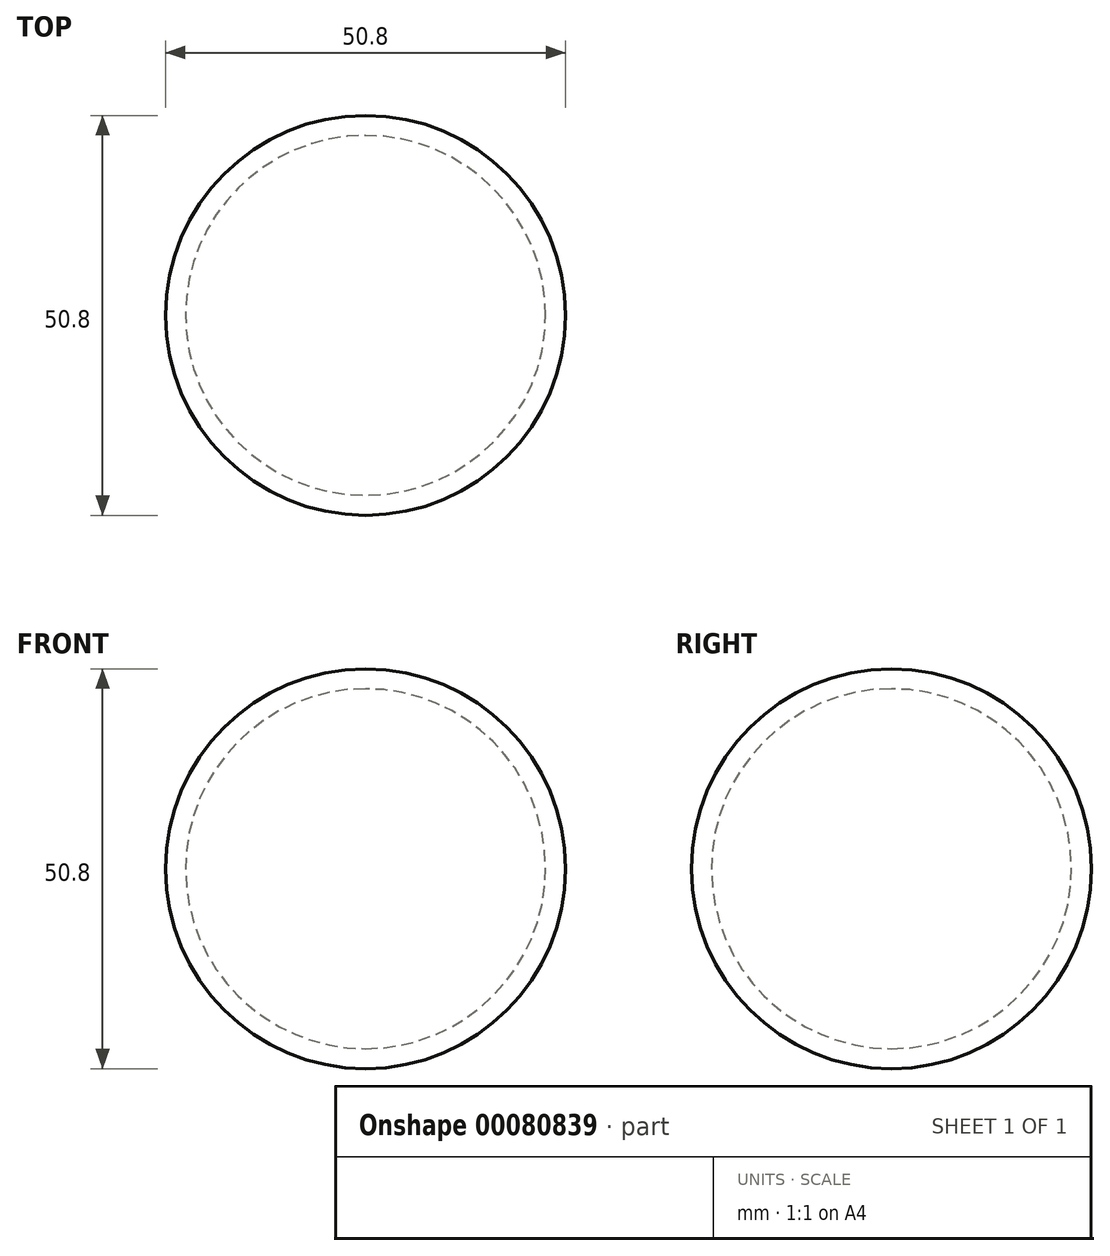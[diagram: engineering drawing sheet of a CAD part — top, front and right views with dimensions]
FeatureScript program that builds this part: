
annotation { "Feature Type Name" : "Feature", "Feature Type Description" : "" }
export const myFeature = defineFeature(function(context is Context, id is Id, definition is map)
    precondition{}
    {
        {
            var Q0;
            Q0=qCreatedBy(makeId("Front.planeOp"),FACE);
            var sketch = newSketch(context, id + "F0", { "sketchPlane" : qUnion([Q0])});
            skArc(sketch, "E0", {"start": v(0, 25.4) * mm, "mid": v(25.4, 0) * mm, "end": v(0, -25.4) * mm});
            skLineSegment(sketch, "E1", {"start": v(0, 25.4) * mm, "end": v(0, -25.4) * mm, "construction": true});
            skArc(sketch, "E2.0", {"start": v(0, 22.86) * mm, "mid": v(22.86, 0) * mm, "end": v(0, -22.86) * mm});
            skLineSegment(sketch, "E3", {"start": v(0, 25.4) * mm, "end": v(0, 22.86) * mm});
            skLineSegment(sketch, "E4", {"start": v(0, -25.4) * mm, "end": v(0, -22.86) * mm});
            skSolve(sketch);
        }
        {
            var Q0;
            Q0 = qSketchRegion(id + "F0", true);
            var Q1;
            Q1=sQuery(id+"F0.wireOp",EDGE,"E1");
            revolve(context, id + "F1", {"entities" : qUnion([Q0]), "axis" : qUnion([Q1]), "revolveType" : RevolveType.FULL});
        }
    });
